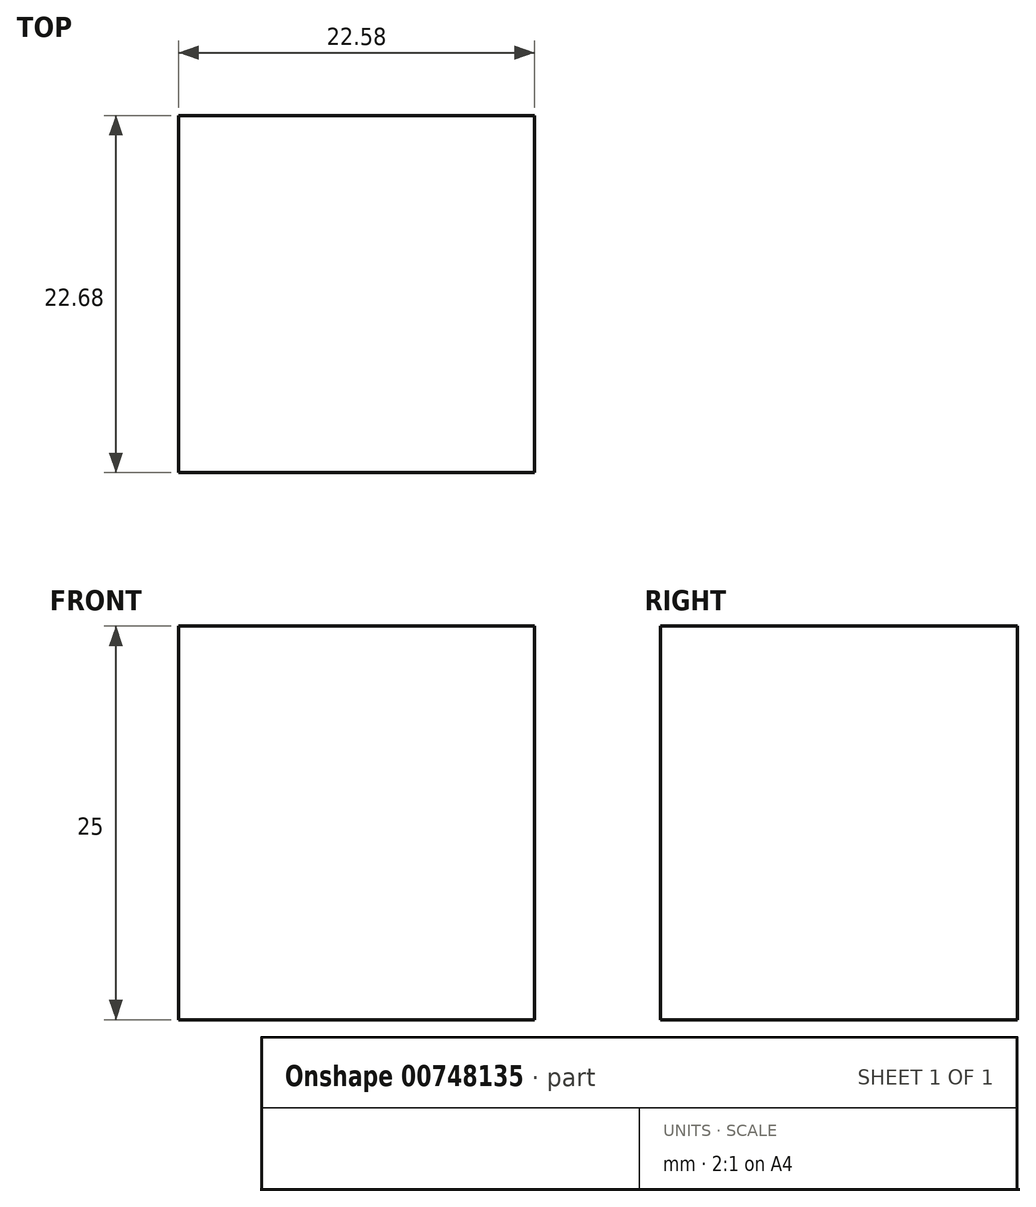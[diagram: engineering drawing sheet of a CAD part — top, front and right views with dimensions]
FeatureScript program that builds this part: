
annotation { "Feature Type Name" : "Feature", "Feature Type Description" : "" }
export const myFeature = defineFeature(function(context is Context, id is Id, definition is map)
    precondition{}
    {
        {
            var Q0;
            Q0=qCreatedBy(makeId("Top.planeOp"),FACE);
            var sketch = newSketch(context, id + "F0", { "sketchPlane" : qUnion([Q0])});
            skLineSegment(sketch, "E0.bottom", {"start": v(-42.38, 41.23) * mm, "end": v(-19.8, 41.23) * mm});
            skLineSegment(sketch, "E0.top", {"start": v(-42.38, 18.55) * mm, "end": v(-19.8, 18.55) * mm});
            skLineSegment(sketch, "E0.left", {"start": v(-42.38, 41.23) * mm, "end": v(-42.38, 18.55) * mm});
            skLineSegment(sketch, "E0.right", {"start": v(-19.8, 41.23) * mm, "end": v(-19.8, 18.55) * mm});
            skSolve(sketch);
        }
        {
            var Q0;
            Q0 = qSketchRegion(id + "F0", true);
            extrude(context, id + "F1", {"entities" : qUnion([Q0]), "depth" : 25 * mm, "offsetDistance" : 25 * mm});
        }
    });
